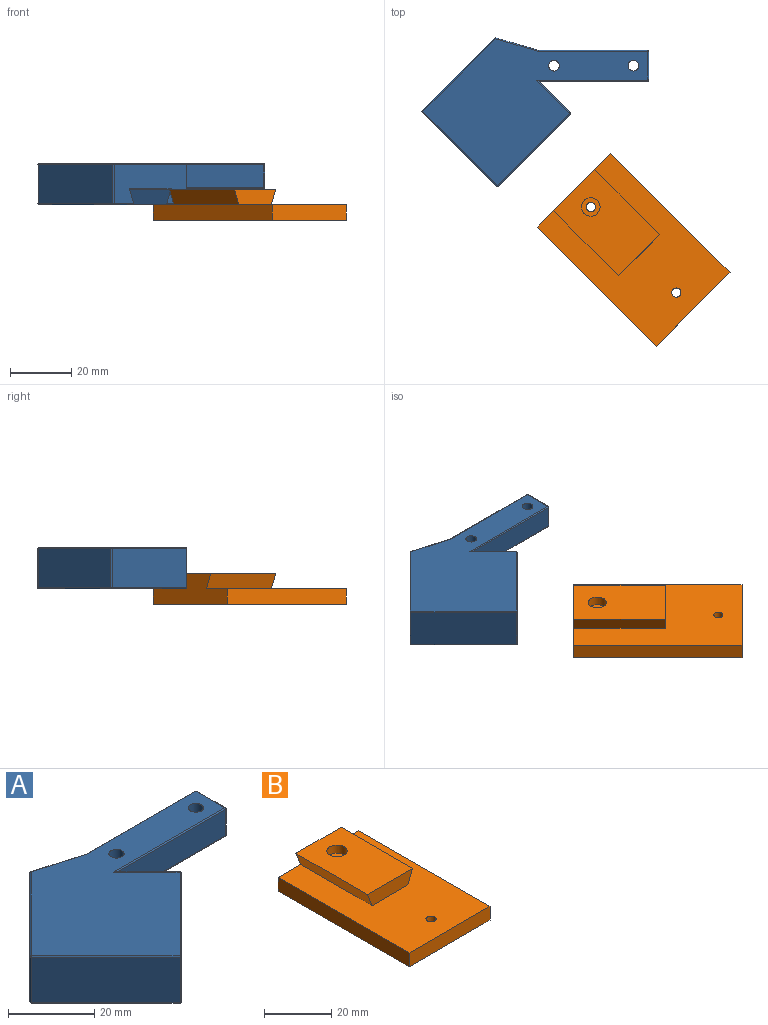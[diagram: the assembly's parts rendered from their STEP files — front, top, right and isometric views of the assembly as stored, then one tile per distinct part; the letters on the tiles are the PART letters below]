
ASSEMBLY  parts=2 mates=2
PART A: 63 faces, bbox 74.3x48.8x13.6 mm
  f0: plane 33.63x9.4mm, normal (0,0,-1), area 274.8mm2, adj f4,f5,f18,f19,f24,f25,f26
  f1: plane 35.7x10.43mm, normal (0,-1,0), area 270mm2, adj f7,f22,f24,f29,f38
  f2: plane 9.4x7.4mm, normal (1,0,0), area 69.6mm2, adj f26,f29,f30,f31
  f3: plane 35.7x10.43mm, normal (0,1,0), area 270mm2, adj f12,f23,f25,f30,f39
  f4: cylinder r=1.75mm len=8mm, axis (0,0,-1), area 88mm2, adj f0,f6
  f5: cylinder r=1.75mm len=8mm, axis (0,0,-1), area 88mm2, adj f0,f6
  f6: plane 73.46x48.03mm, normal (0,0,1), area 1537.3mm2, adj f4,f5,f31,f34,f38,f39,f42,f43
  f7: plane 13x12.07mm, normal (0.71,0.71,0), area 189mm2, adj f1,f18,f21,f22,f43,f52,f57
  f8: plane 24.32x24.32mm, normal (-0.71,-0.71,0), area 439.9mm2, adj f34,f35,f46,f47
  f9: plane 48.03x47.94mm, normal (0,0,-1), area 748.1mm2, adj f13,f15,f36,f47,f51,f54,f57,f58
  f10: plane 23.7x23.7mm, normal (-0.71,0.71,0), area 428.7mm2, adj f45,f46,f53,f54
  f11: plane 2.58x1.68mm, normal (0.71,-0.71,0), area 1mm2, adj f12,f19,f21,f23,f60
  f12: plane 13.97x12.79mm, normal (0.28,0.96,0), area 186.2mm2, adj f3,f11,f44,f53,f58
  f13: plane 22.97x22.61mm, normal (-0.66,-0.66,0.37), area 161.6mm2, adj f9,f14,f16,f17,f51,f61,f62
  f14: plane 34.44x34.44mm, normal (0,0,-1), area 564.3mm2, adj f13,f15,f16,f61
  f15: plane 22.97x22.61mm, normal (0.66,0.66,0.37), area 161.6mm2, adj f9,f14,f16,f17,f36,f61,f62
  f16: plane 13.44x13.44mm, normal (0.71,-0.71,0), area 80.5mm2, adj f13,f14,f15,f62
  f17: plane 23.62x23.62mm, normal (0.71,-0.71,0), area 340.9mm2, adj f13,f15,f35,f36,f42,f51,f52,f61
  f18: cylinder r=5mm len=8.24mm, axis (-0.71,0.71,0), area 25.7mm2, adj f0,f7,f20,f22
  f19: cylinder r=5mm len=8.24mm, axis (0.71,0.71,0), area 25.7mm2, adj f0,f11,f20,f23
  f20: sphere r=5mm, area 46.4mm2, adj f18,f19,f21
  f21: cylinder r=5mm len=7.07mm, axis (0,0,-1), area 0.7mm2, adj f7,f11,f20,f59
  f22: bspline ~8.8x5.3mm, area 5.1mm2, adj f1,f7,f18,f24
  f23: bspline ~8.8x5.53mm, area 5.1mm2, adj f3,f11,f19,f25
  f24: cylinder r=0.3mm len=28.93mm, axis (1,0,0), area 13.6mm2, adj f0,f1,f22,f27
  f25: cylinder r=0.3mm len=28.93mm, axis (-1,0,0), area 13.6mm2, adj f0,f3,f23,f28
  f26: cylinder r=0.3mm len=9.4mm, axis (0,1,0), area 4.4mm2, adj f0,f2,f27,f28
  f27: sphere r=0.3mm, area 0.1mm2, adj f24,f26,f29
  f28: sphere r=0.3mm, area 0.1mm2, adj f25,f26,f30
  f29: cylinder r=0.3mm len=7.4mm, axis (0,0,1), area 3.5mm2, adj f1,f2,f27,f32
  f30: cylinder r=0.3mm len=7.4mm, axis (0,0,-1), area 3.5mm2, adj f2,f3,f28,f33
  f31: cylinder r=0.3mm len=9.4mm, axis (0,-1,0), area 4.4mm2, adj f2,f6,f32,f33
  f32: sphere r=0.3mm, area 0.1mm2, adj f29,f31,f38
  f33: sphere r=0.3mm, area 0.1mm2, adj f30,f31,f39
  f34: cylinder r=0.3mm len=24.54mm, axis (0.71,-0.71,0), area 16.2mm2, adj f6,f8,f37,f40
  f35: cylinder r=0.3mm len=12.79mm, axis (0,0,1), area 6mm2, adj f8,f17,f37,f41
  f36: cylinder r=0.3mm len=6.72mm, axis (-0.71,-0.71,0), area 4.3mm2, adj f9,f15,f17,f41
  f37: sphere r=0.3mm, area 0.1mm2, adj f34,f35,f42
  f38: cylinder r=0.3mm len=36.42mm, axis (-1,0,0), area 17mm2, adj f1,f6,f32,f43
  f39: cylinder r=0.3mm len=35.74mm, axis (1,0,0), area 16.8mm2, adj f3,f6,f33,f44
  f40: sphere r=0.3mm, area 0.2mm2, adj f34,f45,f46
  f41: sphere r=0.3mm, area 0.1mm2, adj f35,f36,f47
  f42: cylinder r=0.3mm len=23.83mm, axis (-0.71,-0.71,0), area 15.7mm2, adj f6,f17,f37,f48
  f43: cylinder r=0.3mm len=11.12mm, axis (0.71,-0.71,0), area 7.1mm2, adj f6,f7,f38,f48
  f44: cylinder r=0.3mm len=14.1mm, axis (-0.96,0.28,0), area 6.9mm2, adj f6,f12,f39,f49
  f45: cylinder r=0.3mm len=23.92mm, axis (-0.71,-0.71,0), area 15.8mm2, adj f6,f10,f40,f49
  f46: cylinder r=0.3mm len=12.79mm, axis (0,0,1), area 6mm2, adj f8,f10,f40,f50
  f47: cylinder r=0.3mm len=24.54mm, axis (-0.71,0.71,0), area 16.2mm2, adj f8,f9,f41,f50
  f48: sphere r=0.3mm, area 0.2mm2, adj f42,f43,f52
  f49: sphere r=0.3mm, area 0.1mm2, adj f44,f45,f53
  f50: sphere r=0.3mm, area 0.2mm2, adj f46,f47,f54
  f51: cylinder r=0.3mm len=6.72mm, axis (-0.71,-0.71,0), area 4.3mm2, adj f9,f13,f17,f55
  f52: cylinder r=0.3mm len=12.79mm, axis (0,0,-1), area 6mm2, adj f7,f17,f48,f55
  f53: cylinder r=0.3mm len=12.79mm, axis (0,0,1), area 4.1mm2, adj f10,f12,f49,f56
  f54: cylinder r=0.3mm len=23.92mm, axis (-0.71,-0.71,0), area 15.8mm2, adj f9,f10,f50,f56
  f55: sphere r=0.3mm, area 0.1mm2, adj f51,f52,f57
  f56: sphere r=0.3mm, area 0.1mm2, adj f53,f54,f58
  f57: cylinder r=0.3mm len=12.07mm, axis (0.71,-0.71,0), area 7.9mm2, adj f7,f9,f55,f59
  f58: cylinder r=0.3mm len=14.06mm, axis (0.96,-0.28,0), area 6.7mm2, adj f9,f12,f56,f60
  f59: torus R=5.3mm, axis (0,0,1), area 3.8mm2, adj f9,f21,f57,f60
  f60: cylinder r=0.3mm len=1.68mm, axis (-0.71,-0.71,0), area 0.9mm2, adj f9,f11,f58,f59
  f61: cylinder r=0.3mm len=13.82mm, axis (-0.71,-0.71,0), area 9mm2, adj f13,f14,f15,f17
  f62: cylinder r=0.3mm len=10.99mm, axis (0.71,0.71,0), area 7.1mm2, adj f9,f13,f15,f16
PART B: 14 faces, bbox 34x55x10 mm
  f0: plane 34x5mm, normal (0,-1,0), area 170mm2, adj f1,f5,f6,f7
  f1: plane 55x5mm, normal (1,0,0), area 275mm2, adj f0,f2,f6,f7
  f2: plane 34x10mm, normal (0,1,0), area 255mm2, adj f1,f5,f6,f7,f8,f9,f10
  f3: cylinder r=1.5mm len=7mm, axis (0,0,-1), area 66mm2, adj f7,f13
  f4: cylinder r=1.5mm len=5mm, axis (0,0,-1), area 47.1mm2, adj f6,f7
  f5: plane 55x5mm, normal (-1,0,0), area 275mm2, adj f0,f2,f6,f7
  f6: plane 55x34mm, normal (0,0,1), area 1412.9mm2, adj f0,f1,f2,f4,f5,f8,f9,f11
  f7: plane 55x34mm, normal (0,0,-1), area 1855.9mm2, adj f0,f1,f2,f3,f4,f5
  f8: plane 30x5mm, normal (0.93,0,-0.37), area 161.6mm2, adj f2,f6,f10,f11
  f9: plane 30x5mm, normal (-0.93,0,-0.37), area 161.6mm2, adj f2,f6,f10,f11
  f10: plane 30x19mm, normal (0,0,1), area 541.7mm2, adj f2,f8,f9,f11,f12
  f11: plane 19x5mm, normal (0,-1,0), area 85mm2, adj f6,f8,f9,f10
  f12: cylinder r=3mm len=6mm, axis (0,0,1), area 56.5mm2, adj f10,f13
  f13: plane 6x6mm, normal (0,0,1), area 21.2mm2, adj f3,f12
PLACE A t=(77.29,-77.47,-12.11)mm
PLACE B rot(axis=(0,0,1),45deg) t=(90.33,-137.55,-22.5)mm
MATE parallel A.f16 <-> B.f2  axis (0.71,-0.71,0) through (36.66,-83.88,-12.5)mm
MATE slider B.f2 <-> A.f16  axis (-0.71,0.71,0) through (70.89,-118.1,-12.5)mm
